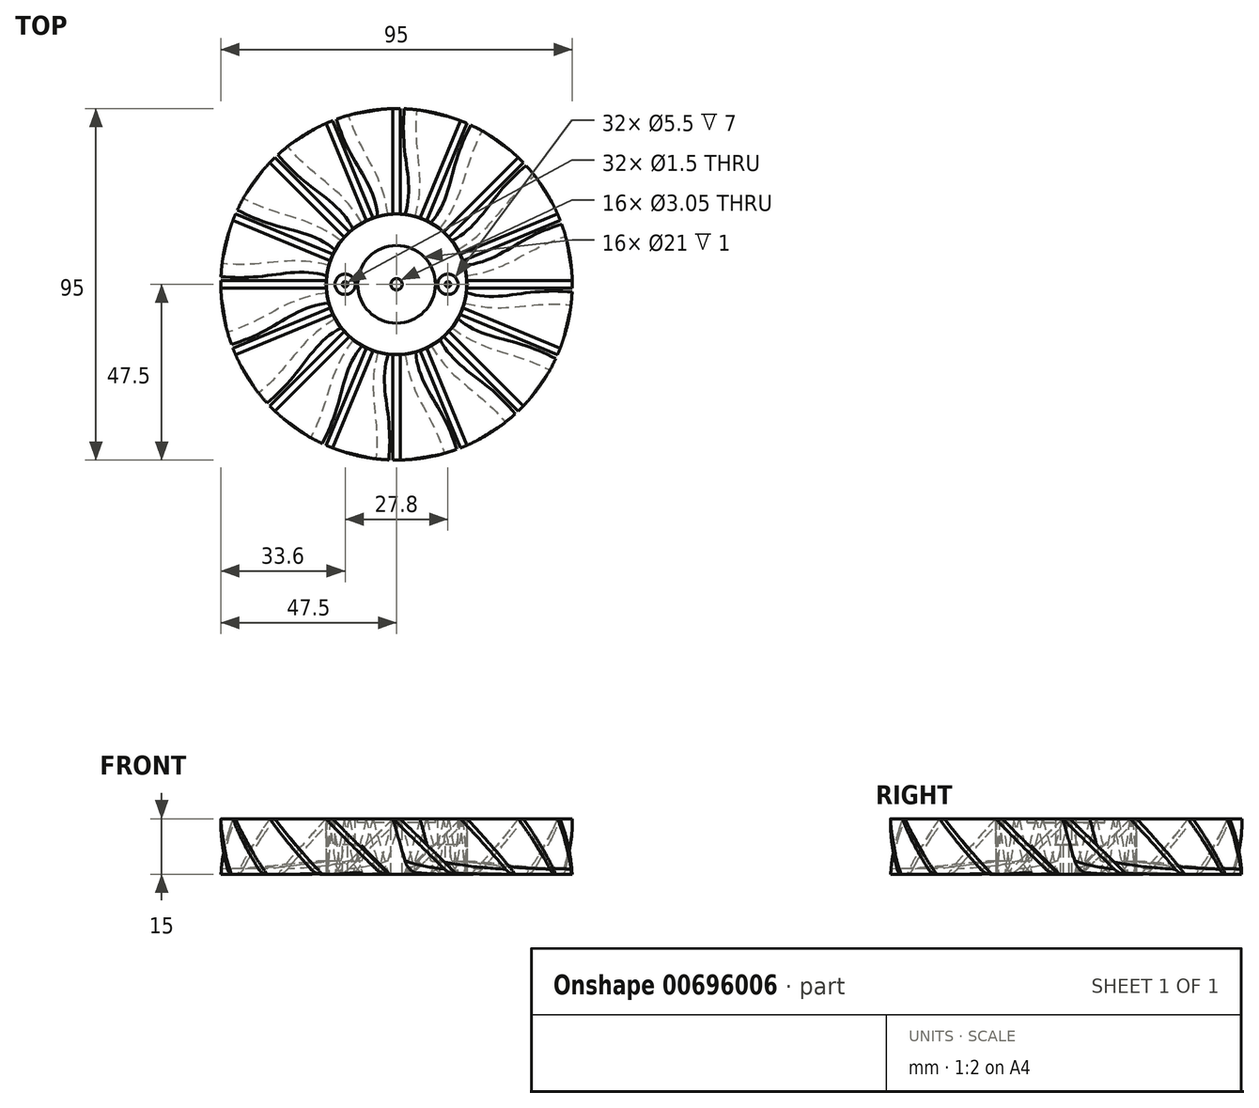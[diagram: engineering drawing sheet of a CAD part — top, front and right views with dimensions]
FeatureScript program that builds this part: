
annotation { "Feature Type Name" : "Feature", "Feature Type Description" : "" }
export const myFeature = defineFeature(function(context is Context, id is Id, definition is map)
    precondition{}
    {
        {
            var Q0;
            Q0=qCreatedBy(makeId("Top.planeOp"),FACE);
            var sketch = newSketch(context, id + "F0", { "sketchPlane" : qUnion([Q0])});
            skCircle(sketch, "E0", {"center": v(0, 0) * mm, "radius": 19 * mm});
            skSolve(sketch);
        }
        {
            var Q0;
            Q0 = qSketchRegion(id + "F0", true);
            extrude(context, id + "F1", {"entities" : qUnion([Q0]), "depth" : 15 * mm, "offsetDistance" : 25 * mm});
        }
        {
            var Q0;
            Q0=makeQuery(id+"F1.opExtrude","CAP_FACE",FACE,{"disambiguationData":[OSD([sQuery(id+"F0.wireOp",EDGE,"E0")])],"isStart":true});
            var sketch = newSketch(context, id + "F2", { "sketchPlane" : qUnion([Q0])});
            skLineSegment(sketch, "E1", {"start": v(0, 0) * mm, "end": v(-3.3, -18.71) * mm});
            skLineSegment(sketch, "E2", {"start": v(0, 0) * mm, "end": v(0, -19) * mm, "construction": true});
            skCircle(sketch, "E3", {"center": v(0, 0) * mm, "radius": 49 * mm, "construction": true});
            skFitSpline(sketch, "E4", {"points": [v(-3.3, -18.71) * mm, v(-14.76, -46.73) * mm], "startDerivative": vector(-6.25, -35.44) * mm, "endDerivative": vector(-12.11, -41.2) * mm});
            skFitSpline(sketch, "E5.0", {"points": [v(-5.27, -18.36) * mm, v(-5.52, -19.77) * mm, v(-6.1, -22.3) * mm, v(-7.22, -25.45) * mm, v(-8.53, -28.26) * mm, v(-10.02, -31) * mm, v(-11.66, -33.93) * mm, v(-13.37, -37.26) * mm, v(-15.07, -41.21) * mm, v(-16.15, -44.4) * mm, v(-16.67, -46.16) * mm]});
            skLineSegment(sketch, "E5.1", {"start": v(-1.97, 0.35) * mm, "end": v(-5.27, -18.36) * mm});
            skLineSegment(sketch, "E6", {"start": v(-14.76, -46.73) * mm, "end": v(-16.67, -46.16) * mm});
            skLineSegment(sketch, "E7", {"start": v(-3.3, -18.71) * mm, "end": v(-4.64, -17.92) * mm});
            skLineSegment(sketch, "E8", {"start": v(-4.64, -17.92) * mm, "end": v(-5.2, -17.92) * mm});
            skLineSegment(sketch, "E9", {"start": v(-5.2, -17.92) * mm, "end": v(-5.27, -18.36) * mm});
            skSolve(sketch);
        }
        {
            var Q0;
            Q0=makeQuery(id+"F1.opExtrude","CAP_FACE",FACE,{"disambiguationData":[OSD([sQuery(id+"F0.wireOp",EDGE,"E0")])],"isStart":false});
            var sketch = newSketch(context, id + "F3", { "sketchPlane" : qUnion([Q0])});
            skLineSegment(sketch, "E10", {"start": v(-0.97, 18.98) * mm, "end": v(0.97, 18.98) * mm});
            skLineSegment(sketch, "E11", {"start": v(0.97, 18.98) * mm, "end": v(0.97, 49) * mm});
            skLineSegment(sketch, "E12", {"start": v(0.97, 49) * mm, "end": v(-0.97, 49) * mm});
            skLineSegment(sketch, "E13", {"start": v(-0.97, 49) * mm, "end": v(-0.97, 18.98) * mm});
            skSolve(sketch);
        }
        {
            var Q1;
            {var subQ4=sQuery(id+"F2.wireOp",EDGE,"E4");Q1=makeQuery(id+"F2.imprint","IMPRINT",FACE,{"disambiguationData":[TD([[makeQuery(id+"F2.imprint","IMPRINT",EDGE,{"derivedFrom":subQ4}),-1.0]])]});}
            var Q2;
            {var subQ0=sQuery(id+"F3.wireOp",EDGE,"E11");Q2=makeQuery(id+"F3.imprint","IMPRINT",FACE,{"disambiguationData":[TD([[makeQuery(id+"F3.imprint","IMPRINT",EDGE,{"derivedFrom":subQ0}),1.0]])]});}
            var Q3;
            Q3=sQuery(id+"F2.wireOp",VERTEX,"E6.end");
            var Q4;
            Q4=sQuery(id+"F3.wireOp",VERTEX,"E13.start");
            loft(context, id + "F4", {"operationType" : NewBodyOperationType.ADD, "sheetProfilesArray" : [{ "sheetProfileEntities" : qUnion([Q1]) }, { "sheetProfileEntities" : qUnion([Q2]) }], "matchConnections" : true, "connections" : [{ "connectionEntities" : qUnion([Q3, Q4]), "connectionEdgeQueries" : qUnion([]), "connectionEdgeParameters" : [] }]});
        }
        {
            var Q0;
            Q0=makeQuery(id+"F4.opLoft","SWEPT_EDGE",EDGE,{"disambiguationData":[OSD([sQuery(id+"F2.wireOp",EDGE,"E4"),sQuery(id+"F2.wireOp",EDGE,"E6"),sQuery(id+"F3.wireOp",EDGE,"E11"),sQuery(id+"F3.wireOp",EDGE,"E12")])]});
            var Q1;
            Q1=makeQuery(id+"F4.opLoft","SWEPT_EDGE",EDGE,{"disambiguationData":[OSD([sQuery(id+"F2.wireOp",EDGE,"E5.0"),sQuery(id+"F2.wireOp",EDGE,"E6"),sQuery(id+"F3.wireOp",EDGE,"E12"),sQuery(id+"F3.wireOp",EDGE,"E13")])]});
            fillet(context, id + "F5", {"entities" : qUnion([Q0, Q1]), "radius" : 1 * mm, "tangentPropagation" : true, "allowEdgeOverflow" : false});
        }
        {
            var Q0;
            Q0=qCreatedBy(makeId("Right.planeOp"),FACE);
            var sketch = newSketch(context, id + "F6", { "sketchPlane" : qUnion([Q0])});
            skLineSegment(sketch, "E14", {"start": v(0, -43.46) * mm, "end": v(0, 53.88) * mm, "construction": true});
            skSolve(sketch);
        }
        {
            var Q0;
            Q0=makeQuery(id+"F1.opExtrude","SWEPT_BODY",BODY,{"disambiguationData":[OSD([sQuery(id+"F0.wireOp",EDGE,"E0")])]});
            var Q1;
            Q1=sQuery(id+"F6.wireOp",EDGE,"E14");
            circularPattern(context, id + "F7", {"entities" : qUnion([Q0]), "axis" : qUnion([Q1]), "angle" : 360 * degree, "instanceCount" : 16, "equalSpace" : true});
        }
        {
            var Q0;
            {var subQ0=sQuery(id+"F3.wireOp",EDGE,"E11");var subQ3=sQuery(id+"F0.wireOp",EDGE,"E0");Q0=makeQuery(id+"F7.opPattern","COPY",FACE,{"derivedFrom":makeQuery(id+"F4.boolean.opBoolean","MERGE",FACE,{"derivedFrom":[makeQuery(id+"F1.opExtrude","CAP_FACE",FACE,{"disambiguationData":[OSD([subQ3])],"isStart":false}),makeQuery(id+"F4.opLoft","CAP_FACE",FACE,{"disambiguationData":[OSD([makeQuery(id+"F3.imprint","IMPRINT",FACE,{"disambiguationData":[TD([[makeQuery(id+"F3.imprint","IMPRINT",EDGE,{"derivedFrom":subQ0}),1.0]])]})])],"isStart":true})]}),"instanceName":"2"});}
            var sketch = newSketch(context, id + "F8", { "sketchPlane" : qUnion([Q0])});
            skCircle(sketch, "E15", {"center": v(0, 0) * mm, "radius": 47.5 * mm});
            skCircle(sketch, "E16", {"center": v(0, 0) * mm, "radius": 52.62 * mm});
            skSolve(sketch);
        }
        {
            var Q0;
            Q0 = qSketchRegion(id + "F8", true);
            extrude(context, id + "F9", {"entities" : qUnion([Q0]), "operationType" : NewBodyOperationType.REMOVE, "endBound" : BoundingType.THROUGH_ALL, "oppositeDirection" : true, "depth" : 15 * mm, "offsetDistance" : 25 * mm});
        }
        {
            var Q0;
            {var subQ0=sQuery(id+"F3.wireOp",EDGE,"E11");var subQ3=sQuery(id+"F0.wireOp",EDGE,"E0");Q0=makeQuery(id+"F7.opPattern","COPY",FACE,{"derivedFrom":makeQuery(id+"F4.boolean.opBoolean","MERGE",FACE,{"derivedFrom":[makeQuery(id+"F1.opExtrude","CAP_FACE",FACE,{"disambiguationData":[OSD([subQ3])],"isStart":false}),makeQuery(id+"F4.opLoft","CAP_FACE",FACE,{"disambiguationData":[OSD([makeQuery(id+"F3.imprint","IMPRINT",FACE,{"disambiguationData":[TD([[makeQuery(id+"F3.imprint","IMPRINT",EDGE,{"derivedFrom":subQ0}),1.0]])]})])],"isStart":true})]}),"instanceName":"11"});}
            var sketch = newSketch(context, id + "F10", { "sketchPlane" : qUnion([Q0])});
            skCircle(sketch, "E17", {"center": v(0, 0) * mm, "radius": 1.52 * mm});
            skSolve(sketch);
        }
        {
            var Q0;
            Q0 = qSketchRegion(id + "F10", true);
            extrude(context, id + "F11", {"entities" : qUnion([Q0]), "operationType" : NewBodyOperationType.REMOVE, "endBound" : BoundingType.THROUGH_ALL, "oppositeDirection" : true, "depth" : 25 * mm, "offsetDistance" : 25 * mm});
        }
        {
            var Q0;
            {var subQ0=sQuery(id+"F3.wireOp",EDGE,"E11");var subQ3=sQuery(id+"F0.wireOp",EDGE,"E0");Q0=makeQuery(id+"F7.opPattern","COPY",FACE,{"derivedFrom":makeQuery(id+"F4.boolean.opBoolean","MERGE",FACE,{"derivedFrom":[makeQuery(id+"F1.opExtrude","CAP_FACE",FACE,{"disambiguationData":[OSD([subQ3])],"isStart":false}),makeQuery(id+"F4.opLoft","CAP_FACE",FACE,{"disambiguationData":[OSD([makeQuery(id+"F3.imprint","IMPRINT",FACE,{"disambiguationData":[TD([[makeQuery(id+"F3.imprint","IMPRINT",EDGE,{"derivedFrom":subQ0}),1.0]])]})])],"isStart":true})]}),"instanceName":"8"});}
            var sketch = newSketch(context, id + "F12", { "sketchPlane" : qUnion([Q0])});
            skLineSegment(sketch, "E18", {"start": v(0, 0) * mm, "end": v(14.1, 0) * mm, "construction": true});
            skLineSegment(sketch, "E19", {"start": v(14.1, 0) * mm, "end": v(-16.8, 0) * mm, "construction": true});
            skCircle(sketch, "E20", {"center": v(-13.9, 0) * mm, "radius": 2.75 * mm});
            skCircle(sketch, "E21", {"center": v(13.9, 0) * mm, "radius": 2.75 * mm});
            skPoint(sketch, "E22", {"position": v(-11.15, 0) * mm});
            skPoint(sketch, "E23", {"position": v(11.15, 0) * mm});
            skCircle(sketch, "E24", {"center": v(0, 0) * mm, "radius": 10.5 * mm});
            skSolve(sketch);
        }
        {
            var Q0;
            Q0=makeQuery(id+"F12.imprint","IMPRINT",FACE,{"disambiguationData":[TD([[makeQuery(id+"F12.imprint","IMPRINT",EDGE,{"derivedFrom":sQuery(id+"F12.wireOp",EDGE,"E24")}),1.0]])]});
            extrude(context, id + "F13", {"entities" : qUnion([Q0]), "operationType" : NewBodyOperationType.REMOVE, "oppositeDirection" : true, "depth" : 1 * mm, "offsetDistance" : 25 * mm});
        }
        {
            var Q0;
            Q0=makeQuery(id+"F12.imprint","IMPRINT",FACE,{"disambiguationData":[TD([[makeQuery(id+"F12.imprint","IMPRINT",EDGE,{"derivedFrom":sQuery(id+"F12.wireOp",EDGE,"E20")}),1.0]])]});
            var Q1;
            Q1=makeQuery(id+"F12.imprint","IMPRINT",FACE,{"disambiguationData":[TD([[makeQuery(id+"F12.imprint","IMPRINT",EDGE,{"derivedFrom":sQuery(id+"F12.wireOp",EDGE,"E21")}),1.0]])]});
            extrude(context, id + "F14", {"entities" : qUnion([Q0, Q1]), "operationType" : NewBodyOperationType.REMOVE, "oppositeDirection" : true, "depth" : 7 * mm, "offsetDistance" : 25 * mm});
        }
        {
            var Q0;
            Q0=makeQuery(id+"F14.boolean.opBoolean","COPY",FACE,{"disambiguationData":[OD(2.0)],"derivedFrom":makeQuery(id+"F14.opExtrude","CAP_FACE",FACE,{"disambiguationData":[OSD([sQuery(id+"F12.wireOp",EDGE,"E20")])],"isStart":false})});
            var sketch = newSketch(context, id + "F15", { "sketchPlane" : qUnion([Q0])});
            skCircle(sketch, "E25", {"center": v(-13.9, 0) * mm, "radius": 0.75 * mm});
            skSolve(sketch);
        }
        {
            var Q0;
            Q0 = qSketchRegion(id + "F15", true);
            extrude(context, id + "F16", {"entities" : qUnion([Q0]), "operationType" : NewBodyOperationType.REMOVE, "oppositeDirection" : true, "depth" : 25 * mm, "offsetDistance" : 25 * mm});
        }
        {
            var Q0;
            Q0=makeQuery(id+"F14.boolean.opBoolean","COPY",FACE,{"disambiguationData":[OD(2.0)],"derivedFrom":makeQuery(id+"F14.opExtrude","CAP_FACE",FACE,{"disambiguationData":[OSD([sQuery(id+"F12.wireOp",EDGE,"E21")])],"isStart":false})});
            var sketch = newSketch(context, id + "F17", { "sketchPlane" : qUnion([Q0])});
            skCircle(sketch, "E26", {"center": v(13.9, 0) * mm, "radius": 0.75 * mm});
            skSolve(sketch);
        }
        {
            var Q0;
            Q0 = qSketchRegion(id + "F17", true);
            extrude(context, id + "F18", {"entities" : qUnion([Q0]), "operationType" : NewBodyOperationType.REMOVE, "oppositeDirection" : true, "depth" : 25 * mm, "offsetDistance" : 25 * mm});
        }
        {
            var Q0;
            Q0=makeQuery(id+"F7.opPattern","COPY",EDGE,{"derivedFrom":makeQuery(id+"F4.opLoft","MID_CAP_EDGE",EDGE,{"disambiguationData":[OSD([sQuery(id+"F0.wireOp",EDGE,"E0"),sQuery(id+"F2.wireOp",EDGE,"E4"),sQuery(id+"F2.wireOp",EDGE,"E6"),sQuery(id+"F2.wireOp",EDGE,"E7")])],"capPos":0.0}),"instanceName":"10"});
            var Q1;
            Q1=makeQuery(id+"F7.opPattern","COPY",EDGE,{"derivedFrom":makeQuery(id+"F4.opLoft","MID_CAP_EDGE",EDGE,{"disambiguationData":[OSD([sQuery(id+"F0.wireOp",EDGE,"E0"),sQuery(id+"F2.wireOp",EDGE,"E4"),sQuery(id+"F2.wireOp",EDGE,"E6"),sQuery(id+"F2.wireOp",EDGE,"E7")])],"capPos":0.0}),"instanceName":"11"});
            var Q2;
            Q2=makeQuery(id+"F7.opPattern","COPY",EDGE,{"derivedFrom":makeQuery(id+"F4.opLoft","MID_CAP_EDGE",EDGE,{"disambiguationData":[OSD([sQuery(id+"F0.wireOp",EDGE,"E0"),sQuery(id+"F2.wireOp",EDGE,"E4"),sQuery(id+"F2.wireOp",EDGE,"E6"),sQuery(id+"F2.wireOp",EDGE,"E7")])],"capPos":0.0}),"instanceName":"12"});
            var Q3;
            Q3=makeQuery(id+"F7.opPattern","COPY",EDGE,{"derivedFrom":makeQuery(id+"F4.opLoft","MID_CAP_EDGE",EDGE,{"disambiguationData":[OSD([sQuery(id+"F0.wireOp",EDGE,"E0"),sQuery(id+"F2.wireOp",EDGE,"E4"),sQuery(id+"F2.wireOp",EDGE,"E6"),sQuery(id+"F2.wireOp",EDGE,"E7")])],"capPos":0.0}),"instanceName":"13"});
            var Q4;
            Q4=makeQuery(id+"F7.opPattern","COPY",EDGE,{"derivedFrom":makeQuery(id+"F4.opLoft","MID_CAP_EDGE",EDGE,{"disambiguationData":[OSD([sQuery(id+"F0.wireOp",EDGE,"E0"),sQuery(id+"F2.wireOp",EDGE,"E4"),sQuery(id+"F2.wireOp",EDGE,"E6"),sQuery(id+"F2.wireOp",EDGE,"E7")])],"capPos":0.0}),"instanceName":"14"});
            var Q5;
            Q5=makeQuery(id+"F7.opPattern","COPY",EDGE,{"derivedFrom":makeQuery(id+"F4.opLoft","MID_CAP_EDGE",EDGE,{"disambiguationData":[OSD([sQuery(id+"F0.wireOp",EDGE,"E0"),sQuery(id+"F2.wireOp",EDGE,"E4"),sQuery(id+"F2.wireOp",EDGE,"E6"),sQuery(id+"F2.wireOp",EDGE,"E7")])],"capPos":0.0}),"instanceName":"15"});
            var Q6;
            Q6=makeQuery(id+"F4.opLoft","MID_CAP_EDGE",EDGE,{"disambiguationData":[OSD([sQuery(id+"F0.wireOp",EDGE,"E0"),sQuery(id+"F2.wireOp",EDGE,"E4"),sQuery(id+"F2.wireOp",EDGE,"E6"),sQuery(id+"F2.wireOp",EDGE,"E7")])],"capPos":0.0});
            var Q7;
            Q7=makeQuery(id+"F7.opPattern","COPY",EDGE,{"derivedFrom":makeQuery(id+"F4.opLoft","MID_CAP_EDGE",EDGE,{"disambiguationData":[OSD([sQuery(id+"F0.wireOp",EDGE,"E0"),sQuery(id+"F2.wireOp",EDGE,"E4"),sQuery(id+"F2.wireOp",EDGE,"E6"),sQuery(id+"F2.wireOp",EDGE,"E7")])],"capPos":0.0}),"instanceName":"1"});
            var Q8;
            Q8=makeQuery(id+"F7.opPattern","COPY",EDGE,{"derivedFrom":makeQuery(id+"F4.opLoft","MID_CAP_EDGE",EDGE,{"disambiguationData":[OSD([sQuery(id+"F0.wireOp",EDGE,"E0"),sQuery(id+"F2.wireOp",EDGE,"E4"),sQuery(id+"F2.wireOp",EDGE,"E6"),sQuery(id+"F2.wireOp",EDGE,"E7")])],"capPos":0.0}),"instanceName":"2"});
            var Q9;
            Q9=makeQuery(id+"F7.opPattern","COPY",EDGE,{"derivedFrom":makeQuery(id+"F4.opLoft","MID_CAP_EDGE",EDGE,{"disambiguationData":[OSD([sQuery(id+"F0.wireOp",EDGE,"E0"),sQuery(id+"F2.wireOp",EDGE,"E4"),sQuery(id+"F2.wireOp",EDGE,"E6"),sQuery(id+"F2.wireOp",EDGE,"E7")])],"capPos":0.0}),"instanceName":"3"});
            var Q10;
            Q10=makeQuery(id+"F7.opPattern","COPY",EDGE,{"derivedFrom":makeQuery(id+"F4.opLoft","MID_CAP_EDGE",EDGE,{"disambiguationData":[OSD([sQuery(id+"F0.wireOp",EDGE,"E0"),sQuery(id+"F2.wireOp",EDGE,"E4"),sQuery(id+"F2.wireOp",EDGE,"E6"),sQuery(id+"F2.wireOp",EDGE,"E7")])],"capPos":0.0}),"instanceName":"4"});
            var Q11;
            Q11=makeQuery(id+"F7.opPattern","COPY",EDGE,{"derivedFrom":makeQuery(id+"F4.opLoft","MID_CAP_EDGE",EDGE,{"disambiguationData":[OSD([sQuery(id+"F0.wireOp",EDGE,"E0"),sQuery(id+"F2.wireOp",EDGE,"E4"),sQuery(id+"F2.wireOp",EDGE,"E6"),sQuery(id+"F2.wireOp",EDGE,"E7")])],"capPos":0.0}),"instanceName":"5"});
            var Q12;
            Q12=makeQuery(id+"F7.opPattern","COPY",EDGE,{"derivedFrom":makeQuery(id+"F4.opLoft","MID_CAP_EDGE",EDGE,{"disambiguationData":[OSD([sQuery(id+"F0.wireOp",EDGE,"E0"),sQuery(id+"F2.wireOp",EDGE,"E4"),sQuery(id+"F2.wireOp",EDGE,"E6"),sQuery(id+"F2.wireOp",EDGE,"E7")])],"capPos":0.0}),"instanceName":"6"});
            var Q13;
            Q13=makeQuery(id+"F7.opPattern","COPY",EDGE,{"derivedFrom":makeQuery(id+"F4.opLoft","MID_CAP_EDGE",EDGE,{"disambiguationData":[OSD([sQuery(id+"F0.wireOp",EDGE,"E0"),sQuery(id+"F2.wireOp",EDGE,"E4"),sQuery(id+"F2.wireOp",EDGE,"E6"),sQuery(id+"F2.wireOp",EDGE,"E7")])],"capPos":0.0}),"instanceName":"7"});
            var Q14;
            Q14=makeQuery(id+"F7.opPattern","COPY",EDGE,{"derivedFrom":makeQuery(id+"F4.opLoft","MID_CAP_EDGE",EDGE,{"disambiguationData":[OSD([sQuery(id+"F0.wireOp",EDGE,"E0"),sQuery(id+"F2.wireOp",EDGE,"E4"),sQuery(id+"F2.wireOp",EDGE,"E6"),sQuery(id+"F2.wireOp",EDGE,"E7")])],"capPos":0.0}),"instanceName":"8"});
            var Q15;
            Q15=makeQuery(id+"F7.opPattern","COPY",EDGE,{"derivedFrom":makeQuery(id+"F4.opLoft","MID_CAP_EDGE",EDGE,{"disambiguationData":[OSD([sQuery(id+"F0.wireOp",EDGE,"E0"),sQuery(id+"F2.wireOp",EDGE,"E4"),sQuery(id+"F2.wireOp",EDGE,"E6"),sQuery(id+"F2.wireOp",EDGE,"E7")])],"capPos":0.0}),"instanceName":"9"});
            fillet(context, id + "F19", {"entities" : qUnion([Q0, Q1, Q2, Q3, Q4, Q5, Q6, Q7, Q8, Q9, Q10, Q11, Q12, Q13, Q14, Q15]), "radius" : 5 * mm, "tangentPropagation" : true, "allowEdgeOverflow" : false});
        }
    });
